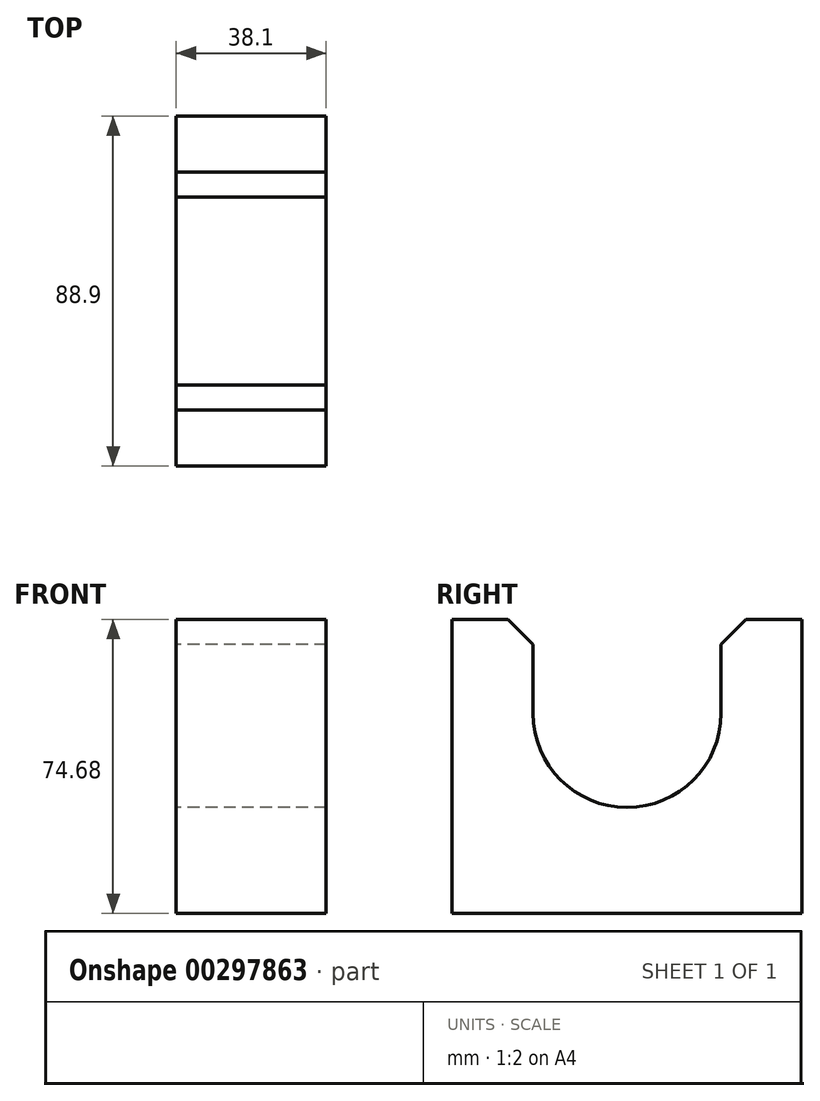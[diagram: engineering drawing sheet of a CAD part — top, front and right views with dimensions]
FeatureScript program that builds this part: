
annotation { "Feature Type Name" : "Feature", "Feature Type Description" : "" }
export const myFeature = defineFeature(function(context is Context, id is Id, definition is map)
    precondition{}
    {
        {
            var Q0;
            Q0=qCreatedBy(makeId("Right.planeOp"),FACE);
            var sketch = newSketch(context, id + "F0", { "sketchPlane" : qUnion([Q0])});
            skArc(sketch, "E0", {"start": v(-23.88, 0) * mm, "mid": v(0, -23.88) * mm, "end": v(23.88, 0) * mm});
            skLineSegment(sketch, "E1.top", {"start": v(-44.45, -50.8) * mm, "end": v(44.45, -50.8) * mm});
            skLineSegment(sketch, "E1.left", {"start": v(-44.45, 23.88) * mm, "end": v(-44.45, -50.8) * mm});
            skLineSegment(sketch, "E1.right", {"start": v(44.45, 23.88) * mm, "end": v(44.45, -50.8) * mm});
            skLineSegment(sketch, "E2", {"start": v(44.45, 23.88) * mm, "end": v(23.88, 23.88) * mm});
            skPoint(sketch, "E3.orphan", {"position": v(0, 23.88) * mm});
            skLineSegment(sketch, "E4", {"start": v(-23.88, 0) * mm, "end": v(-23.88, 23.88) * mm});
            skLineSegment(sketch, "E5", {"start": v(23.88, 0) * mm, "end": v(23.88, 23.88) * mm});
            skPoint(sketch, "E6.orphan", {"position": v(44.45, 50.8) * mm});
            skLineSegment(sketch, "E7.trimOffspring", {"start": v(-23.88, 23.88) * mm, "end": v(-44.45, 23.88) * mm});
            skPoint(sketch, "E8.orphan", {"position": v(-44.45, 50.8) * mm});
            skSolve(sketch);
        }
        {
            var Q0;
            Q0 = qSketchRegion(id + "F0", true);
            extrude(context, id + "F1", {"entities" : qUnion([Q0]), "depth" : 38.1 * mm});
        }
        {
            var Q0;
            Q0=makeQuery(id+"F1.opExtrude","SWEPT_EDGE",EDGE,{"disambiguationData":[OSD([sQuery(id+"F0.wireOp",EDGE,"E4"),sQuery(id+"F0.wireOp",EDGE,"E7.trimOffspring")])]});
            var Q1;
            Q1=makeQuery(id+"F1.opExtrude","SWEPT_EDGE",EDGE,{"disambiguationData":[OSD([sQuery(id+"F0.wireOp",EDGE,"E2"),sQuery(id+"F0.wireOp",EDGE,"E5")])]});
            chamfer(context, id + "F2", {"entities" : qUnion([Q0, Q1]), "width" : 6.35 * mm, "tangentPropagation" : true});
        }
    });
